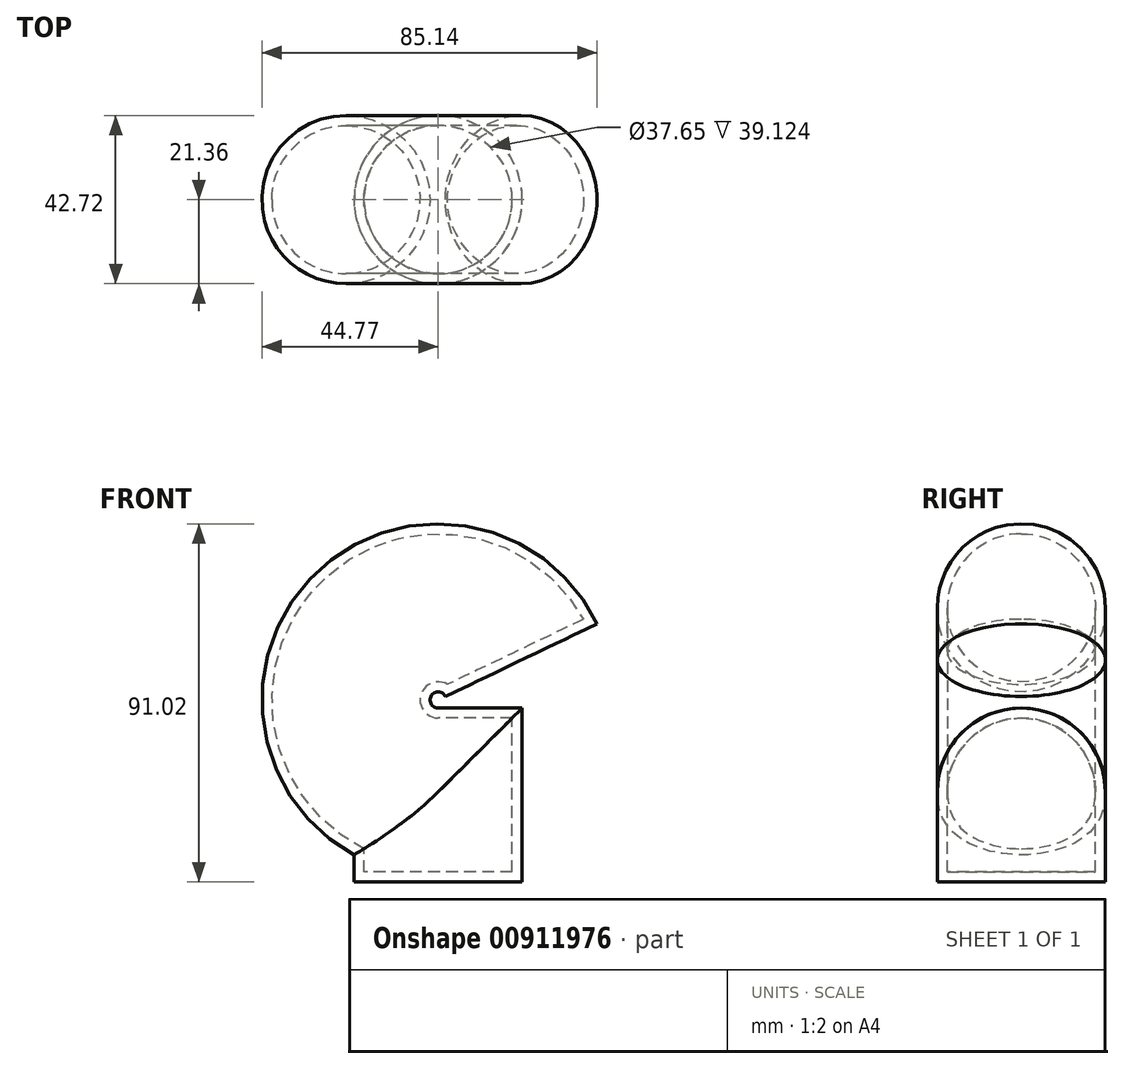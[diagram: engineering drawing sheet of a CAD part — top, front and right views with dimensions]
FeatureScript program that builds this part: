
annotation { "Feature Type Name" : "Feature", "Feature Type Description" : "" }
export const myFeature = defineFeature(function(context is Context, id is Id, definition is map)
    precondition{}
    {
        {
            var Q0;
            Q0=qCreatedBy(makeId("Top.planeOp"),FACE);
            var sketch = newSketch(context, id + "F0", { "sketchPlane" : qUnion([Q0])});
            skCircle(sketch, "E0", {"center": v(0, 0) * mm, "radius": 21.36 * mm});
            skSolve(sketch);
        }
        {
            var Q0;
            Q0=qCreatedBy(makeId("Front.planeOp"),FACE);
            var sketch = newSketch(context, id + "F1", { "sketchPlane" : qUnion([Q0])});
            skLineSegment(sketch, "E1", {"start": v(0, 0) * mm, "end": v(0, 22.84) * mm});
            skArc(sketch, "E2", {"start": v(21.1, 56.37) * mm, "mid": v(-19.81, 58.72) * mm, "end": v(0, 22.84) * mm});
            skSolve(sketch);
        }
        {
            var Q0;
            Q0=makeQuery(id+"F0.imprint","IMPRINT",FACE,{"disambiguationData":[TD([[makeQuery(id+"F0.imprint","IMPRINT",EDGE,{"derivedFrom":sQuery(id+"F0.wireOp",EDGE,"E0")}),1.0]])]});
            var Q1;
            Q1=sQuery(id+"F1.wireOp",EDGE,"E1");
            var Q2;
            Q2=sQuery(id+"F1.wireOp",EDGE,"E2");
            sweep(context, id + "F2", {"profiles" : qUnion([Q0]), "path" : qUnion([Q1, Q2])});
        }
        {
            var Q0;
            Q0=makeQuery(id+"F2.opSweep","CAP_FACE",FACE,{"disambiguationData":[OSD([sQuery(id+"F0.wireOp",EDGE,"E0"),sQuery(id+"F1.wireOp",VERTEX,"E2.start")])],"isStart":false});
            var Q1;
            Q1=makeQuery(id+"F2.opSweep","SWEPT_BODY",BODY,{"disambiguationData":[OSD([sQuery(id+"F0.wireOp",EDGE,"E0"),sQuery(id+"F1.wireOp",EDGE,"E2")])]});
            shell(context, id + "F3", {"isHollow" : true, "entities" : qUnion([Q0]), "parts" : qUnion([Q1]), "thickness" : 2.54 * mm});
        }
    });
